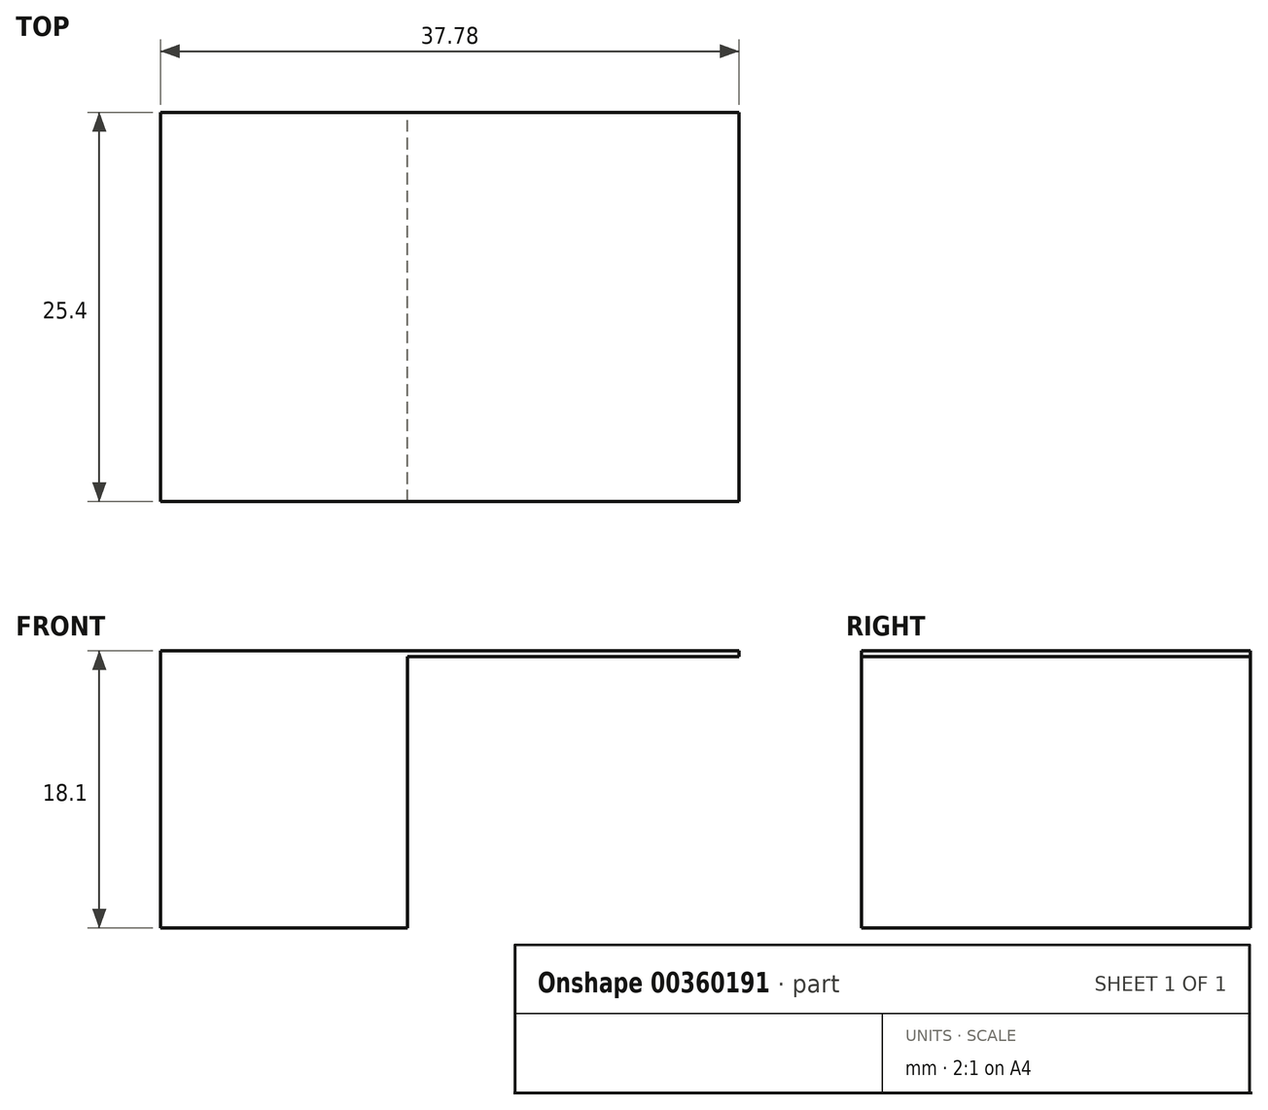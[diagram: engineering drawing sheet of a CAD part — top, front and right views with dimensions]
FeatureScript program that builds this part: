
annotation { "Feature Type Name" : "Feature", "Feature Type Description" : "" }
export const myFeature = defineFeature(function(context is Context, id is Id, definition is map)
    precondition{}
    {
        {
            var Q0;
            Q0=qCreatedBy(makeId("Front.planeOp"),FACE);
            var sketch = newSketch(context, id + "F0", { "sketchPlane" : qUnion([Q0])});
            skLineSegment(sketch, "E0.bottom", {"start": v(-21.64, 17.7) * mm, "end": v(-59.42, 17.7) * mm});
            skLineSegment(sketch, "E0.top", {"start": v(-21.64, 35.81) * mm, "end": v(-59.42, 35.81) * mm});
            skLineSegment(sketch, "E0.left", {"start": v(-21.64, 17.7) * mm, "end": v(-21.64, 35.81) * mm});
            skLineSegment(sketch, "E0.right", {"start": v(-59.42, 17.7) * mm, "end": v(-59.42, 35.81) * mm});
            skPoint(sketch, "E0.middle", {"position": v(-40.53, 26.76) * mm});
            skLineSegment(sketch, "E1.bottom", {"start": v(0, 0) * mm, "end": v(-43.29, 0) * mm});
            skLineSegment(sketch, "E1.top", {"start": v(0, 35.42) * mm, "end": v(-43.29, 35.42) * mm});
            skLineSegment(sketch, "E1.left", {"start": v(0, 0) * mm, "end": v(0, 35.42) * mm});
            skLineSegment(sketch, "E1.right", {"start": v(-43.29, 0) * mm, "end": v(-43.29, 35.42) * mm});
            skPoint(sketch, "E1.middle", {"position": v(-21.64, 17.7) * mm});
            skSolve(sketch);
        }
        {
            var Q0;
            {var subQ2=sQuery(id+"F0.wireOp",EDGE,"E0.top");Q0=makeQuery(id+"F0.imprint","IMPRINT",FACE,{"disambiguationData":[TD([[makeQuery(id+"F0.imprint","IMPRINT",EDGE,{"derivedFrom":subQ2}),1.0]])]});}
            extrude(context, id + "F1", {"entities" : qUnion([Q0]), "depth" : 25.4 * mm});
        }
    });
